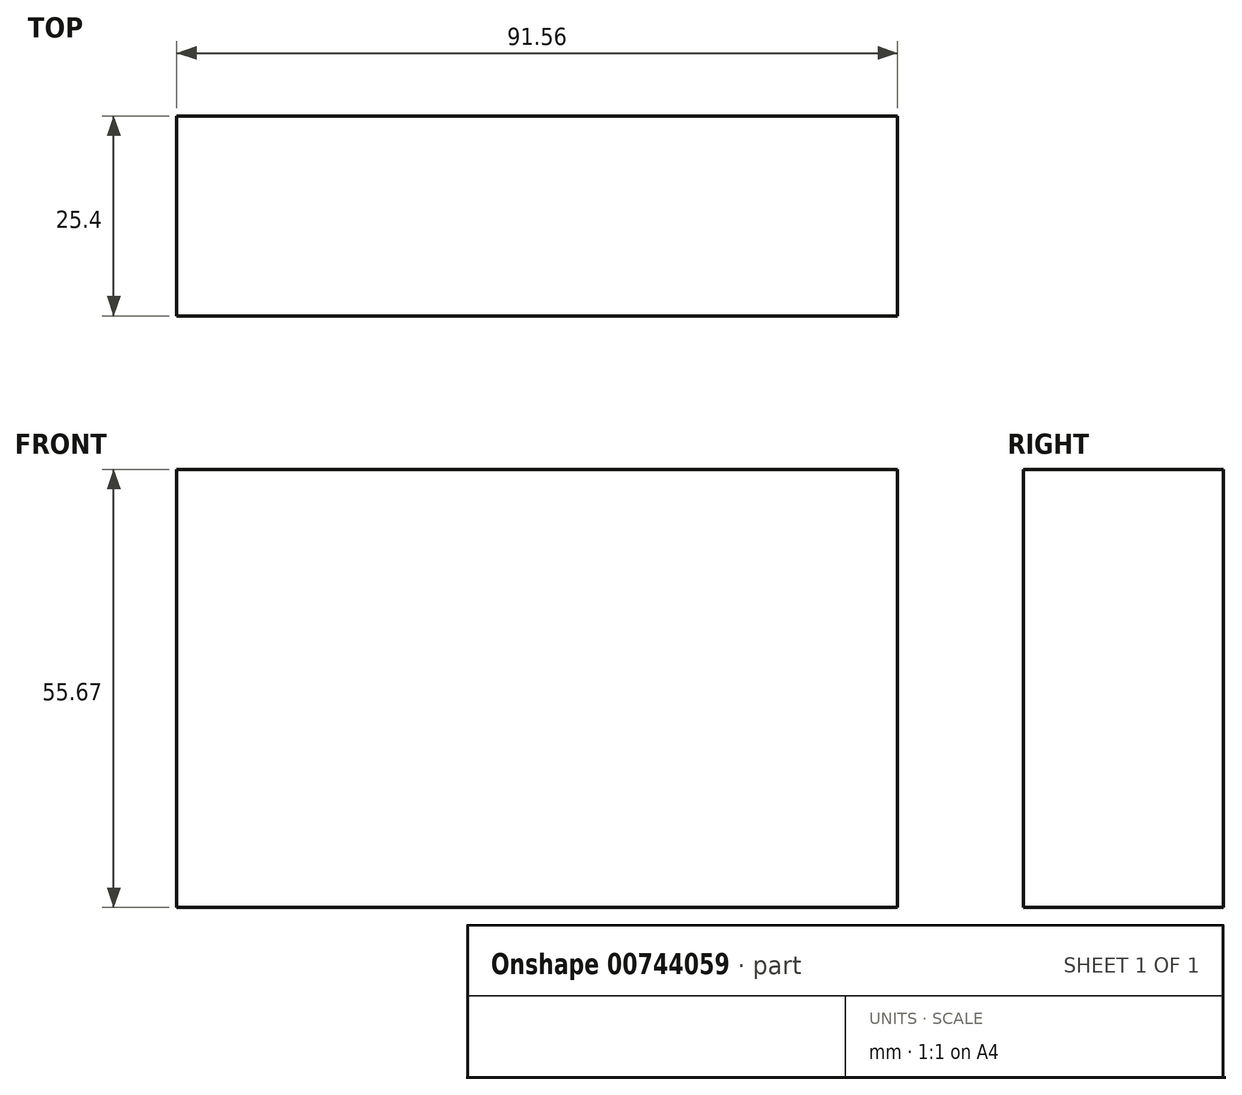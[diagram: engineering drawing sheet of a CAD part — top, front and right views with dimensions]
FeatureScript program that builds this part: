
annotation { "Feature Type Name" : "Feature", "Feature Type Description" : "" }
export const myFeature = defineFeature(function(context is Context, id is Id, definition is map)
    precondition{}
    {
        {
            var Q0;
            Q0=qCreatedBy(makeId("Front.planeOp"),FACE);
            var sketch = newSketch(context, id + "F0", { "sketchPlane" : qUnion([Q0])});
            skPoint(sketch, "E0.0", {"position": v(0, 0) * mm});
            skLineSegment(sketch, "E1.bottom", {"start": v(46.19, 34.59) * mm, "end": v(-45.37, 34.59) * mm});
            skLineSegment(sketch, "E1.top", {"start": v(46.19, -21.08) * mm, "end": v(-45.37, -21.08) * mm});
            skLineSegment(sketch, "E1.left", {"start": v(46.19, 34.59) * mm, "end": v(46.19, -21.08) * mm});
            skLineSegment(sketch, "E1.right", {"start": v(-45.37, 34.59) * mm, "end": v(-45.37, -21.08) * mm});
            skSolve(sketch);
        }
        {
            var Q0;
            Q0=sQuery(id+"F0.wireOp",EDGE,"E1.bottom");
            var Q1;
            Q1 = qBodyType(qCreatedBy(id + "F0" ,EDGE), BodyType.WIRE);
            extrude(context, id + "F1", {"bodyType" : ToolBodyType.SURFACE, "surfaceEntities" : qUnion([Q0, Q1]), "depth" : 25.4 * mm, "offsetDistance" : 25.4 * mm});
        }
    });
